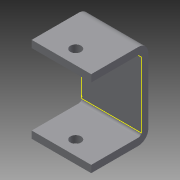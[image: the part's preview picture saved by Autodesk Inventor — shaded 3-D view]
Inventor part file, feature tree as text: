
AUTODESK INVENTOR PART (.ipt)
format: ipt  version: 2013 (Build 170138000, 138)  size: 139,264 bytes
history: native  units: in
note: dims shown in document units (in); Inventor stores cm internally (conversion verified against a paired STEP export)
features: sheet_metal_op x4, sketch x4, other x3, extrude x1
ambient origin geometry x8: Origin, YZ Plane, XZ Plane, XY Plane, X Axis, Y Axis, Z Axis, Center Point
bodies: Solid1 (feature_tree)
feature tree (12):
  sheet_metal_op  "Face1"
  sheet_metal_op  "Flange1"
  extrude  "Extrusion1"  Depth=1.15in
  sketch  "Sketch1"  dims[d4=0.5788in d5=1.15in]
  other  "Plate1"
  sketch  "Sketch2"  dims[d6=0.125in]
  other  "Plate2"
  sheet_metal_op  "Bend1"
  sheet_metal_op  "Corner1"
  sketch  "Sketch3"  dims[d7=0.125in]
  sketch  "Sketch9"  dims[d8=0.0625in d9=0.25in d10=0.125in d11=1.0in d12=90.0deg d13=0.05in d14=0.5in d15=0.125in d16=0.125in d17=0.25in d18=0.1875in d19=2999.0in d20=0.0in d21=0.575in d31=0.266in d33=0.266in d34=0.188in d35=0.125in d36=0.0in d37=0.316in d38=0.442in]
  other  "Cut4"
